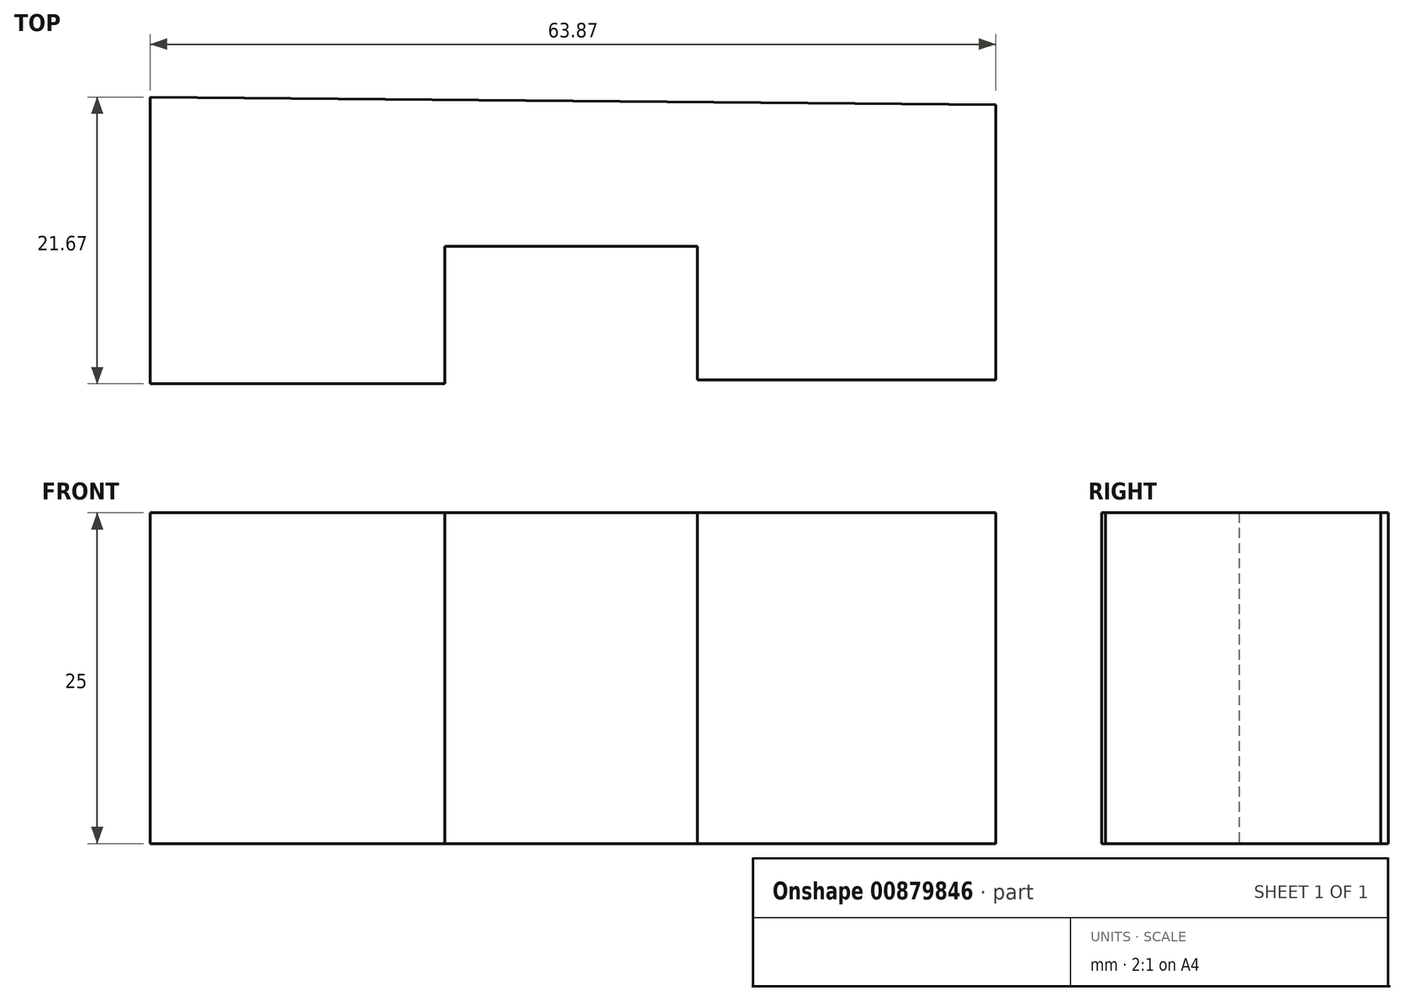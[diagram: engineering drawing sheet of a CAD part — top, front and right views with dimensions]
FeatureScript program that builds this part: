
annotation { "Feature Type Name" : "Feature", "Feature Type Description" : "" }
export const myFeature = defineFeature(function(context is Context, id is Id, definition is map)
    precondition{}
    {
        {
            var Q0;
            Q0=qCreatedBy(makeId("Top.planeOp"),FACE);
            var sketch = newSketch(context, id + "F0", { "sketchPlane" : qUnion([Q0])});
            skLineSegment(sketch, "E0", {"start": v(-53.9, 11.27) * mm, "end": v(-53.9, -10.4) * mm});
            skLineSegment(sketch, "E1", {"start": v(-53.9, -10.4) * mm, "end": v(-31.64, -10.4) * mm});
            skLineSegment(sketch, "E2", {"start": v(-31.64, -10.4) * mm, "end": v(-31.64, 0) * mm});
            skLineSegment(sketch, "E3", {"start": v(-31.64, 0) * mm, "end": v(-12.57, 0) * mm});
            skLineSegment(sketch, "E4", {"start": v(-12.57, 0) * mm, "end": v(-12.57, -10.11) * mm});
            skLineSegment(sketch, "E5", {"start": v(-12.57, -10.11) * mm, "end": v(9.97, -10.11) * mm});
            skLineSegment(sketch, "E6", {"start": v(9.97, -10.11) * mm, "end": v(9.97, 10.7) * mm});
            skLineSegment(sketch, "E7", {"start": v(9.97, 10.7) * mm, "end": v(-53.9, 11.27) * mm});
            skSolve(sketch);
        }
        {
            var Q0;
            Q0 = qSketchRegion(id + "F0", true);
            extrude(context, id + "F1", {"entities" : qUnion([Q0]), "depth" : 25 * mm, "offsetDistance" : 25 * mm});
        }
    });
